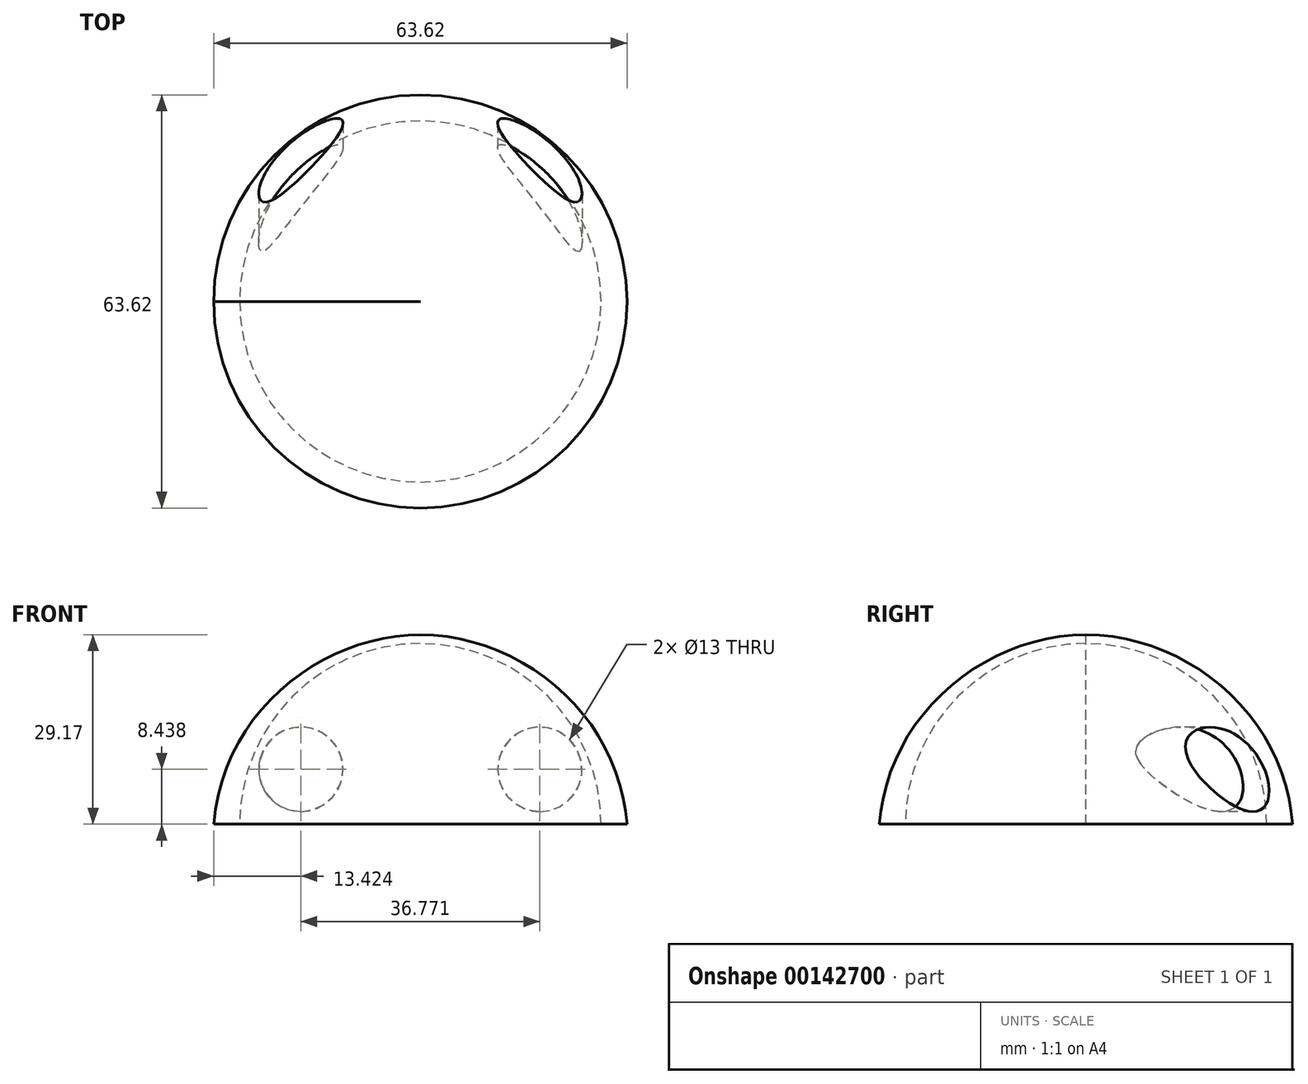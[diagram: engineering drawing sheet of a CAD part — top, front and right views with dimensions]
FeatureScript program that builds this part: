
annotation { "Feature Type Name" : "Feature", "Feature Type Description" : "" }
export const myFeature = defineFeature(function(context is Context, id is Id, definition is map)
    precondition{}
    {
        {
            var Q0;
            Q0=qCreatedBy(makeId("Front.planeOp"),FACE);
            var sketch = newSketch(context, id + "F0", { "sketchPlane" : qUnion([Q0])});
            skLineSegment(sketch, "E0", {"start": v(-32.2, 0) * mm, "end": v(31.8, 0) * mm});
            skCircle(sketch, "E1", {"center": v(-18.39, 8.44) * mm, "radius": 6.5 * mm});
            skLineSegment(sketch, "E2", {"start": v(0, 0) * mm, "end": v(0, 29.17) * mm});
            skCircle(sketch, "E3.MirrorC", {"center": v(18.39, 8.44) * mm, "radius": 6.5 * mm});
            skFitSpline(sketch, "E4", {"points": [v(31.8, 0) * mm, v(0, 29.17) * mm], "startDerivative": vector(-4.44, 53.57) * mm, "endDerivative": vector(-43.63, 0) * mm});
            skFitSpline(sketch, "E5.MirrorCS", {"points": [v(-31.8, 0) * mm, v(0, 29.17) * mm], "startDerivative": vector(4.44, 53.57) * mm, "endDerivative": vector(43.63, 0) * mm});
            skSolve(sketch);
        }
        {
            var Q0;
            Q0=makeQuery(id+"F0.imprint","IMPRINT",FACE,{"disambiguationData":[TD([[makeQuery(id+"F0.imprint","IMPRINT",EDGE,{"derivedFrom":sQuery(id+"F0.wireOp",EDGE,"E1")}),-1.0]])]});
            var Q1;
            Q1=sQuery(id+"F0.wireOp",EDGE,"E2");
            revolve(context, id + "F1", {"entities" : qUnion([Q0]), "axis" : qUnion([Q1]), "revolveType" : RevolveType.FULL});
        }
        {
            var Q0;
            Q0=sQuery(id+"F0.wireOp",VERTEX,"E3.MirrorC.center");
            var Q1;
            Q1=sQuery(id+"F0.wireOp",VERTEX,"E1.center");
            var Q2;
            Q2=makeQuery(id+"F1.opRevolve","SWEPT_BODY",BODY,{"disambiguationData":[OSD([sQuery(id+"F0.wireOp",EDGE,"E0"),sQuery(id+"F0.wireOp",EDGE,"E1"),sQuery(id+"F0.wireOp",EDGE,"KgA8QQNy-DM4i-AKen-ou29-VIGATs0A9gmJ"),sQuery(id+"F0.wireOp",EDGE,"E2")])]});
            hole(context, id + "F2", {"style" : HoleStyle.SIMPLE, "endStyle" : HoleEndStyle.THROUGH, "holeDiameter" : 13 * mm, "locations" : qUnion([Q0, Q1]), "scope" : qUnion([Q2]), "isTappedThrough" : true});
        }
        {
            var Q0;
            Q0=makeQuery(id+"F1.opRevolve","SWEPT_FACE",FACE,{"disambiguationData":[OSD([sQuery(id+"F0.wireOp",EDGE,"E0")])]});
            var sketch = newSketch(context, id + "F3", { "sketchPlane" : qUnion([Q0])});
            skCircle(sketch, "E6.0", {"center": v(0, 0) * mm, "radius": 27.8 * mm});
            skLineSegment(sketch, "E7", {"start": v(-27.8, 0) * mm, "end": v(27.8, 0) * mm});
            skSolve(sketch);
        }
        {
            var Q0;
            {var subQ0=sQuery(id+"F3.wireOp",EDGE,"E7");Q0=makeQuery(id+"F3.imprint","IMPRINT",FACE,{"disambiguationData":[TD([[makeQuery(id+"F3.imprint","IMPRINT",EDGE,{"derivedFrom":subQ0}),-1.0]])]});}
            var Q1;
            Q1=sQuery(id+"F3.wireOp",EDGE,"E7");
            revolve(context, id + "F4", {"operationType" : NewBodyOperationType.REMOVE, "entities" : qUnion([Q0]), "axis" : qUnion([Q1]), "revolveType" : RevolveType.FULL, "oppositeDirection" : true});
        }
    });
